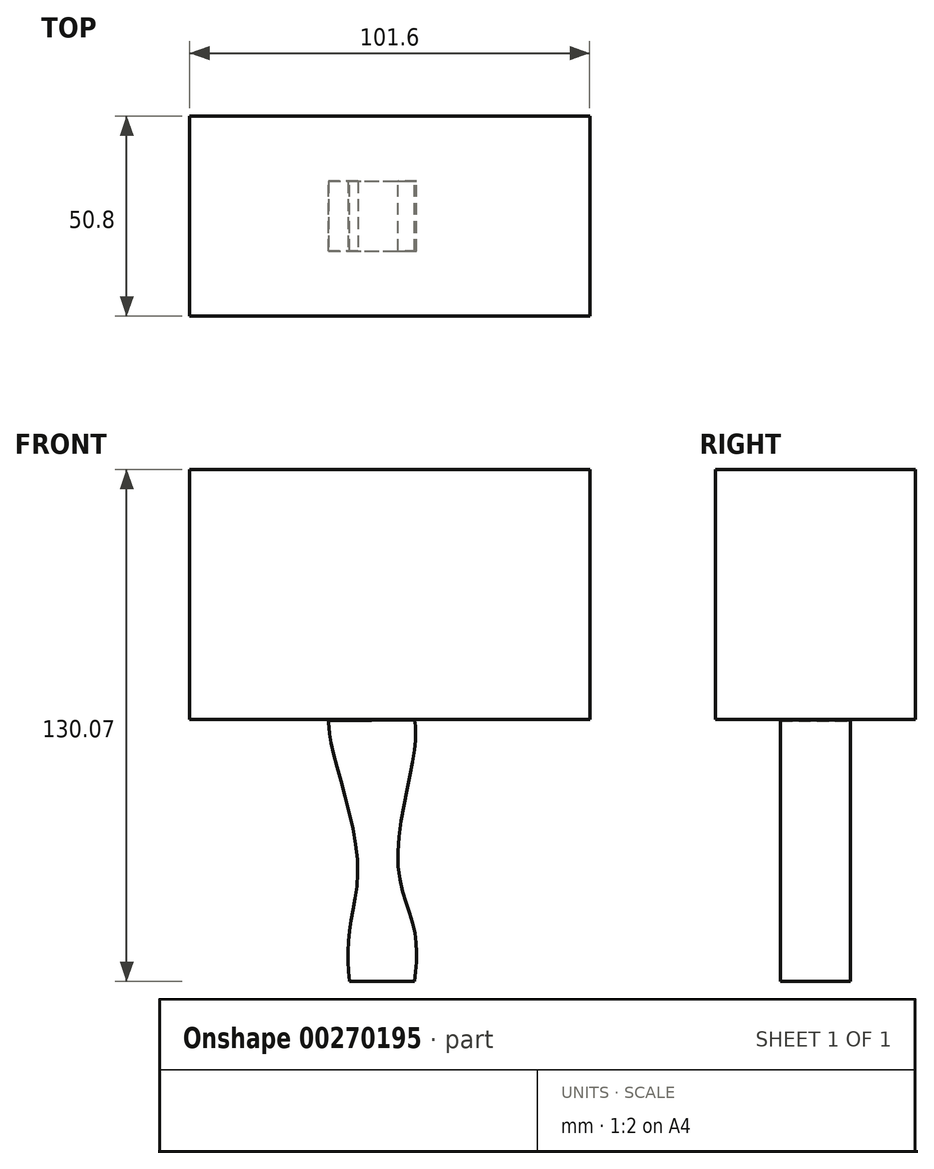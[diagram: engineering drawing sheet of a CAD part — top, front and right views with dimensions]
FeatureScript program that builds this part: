
annotation { "Feature Type Name" : "Feature", "Feature Type Description" : "" }
export const myFeature = defineFeature(function(context is Context, id is Id, definition is map)
    precondition{}
    {
        {
            var Q0;
            Q0=qCreatedBy(makeId("Front.planeOp"),FACE);
            var sketch = newSketch(context, id + "F0", { "sketchPlane" : qUnion([Q0])});
            skLineSegment(sketch, "E0.bottom", {"start": v(-47.1, 68.51) * mm, "end": v(54.5, 68.51) * mm});
            skLineSegment(sketch, "E0.top", {"start": v(-47.1, 5.01) * mm, "end": v(54.5, 5.01) * mm});
            skLineSegment(sketch, "E0.left", {"start": v(-47.1, 68.51) * mm, "end": v(-47.1, 5.01) * mm});
            skLineSegment(sketch, "E0.right", {"start": v(54.5, 68.51) * mm, "end": v(54.5, 5.01) * mm});
            skSolve(sketch);
        }
        {
            var Q0;
            Q0=makeQuery(id+"F0.imprint","IMPRINT",FACE,{"disambiguationData":[TD([[makeQuery(id+"F0.imprint","IMPRINT",EDGE,{"derivedFrom":sQuery(id+"F0.wireOp",EDGE,"E0.bottom")}),-1.0]])]});
            extrude(context, id + "F1", {"entities" : qUnion([Q0]), "endBound" : BoundingType.SYMMETRIC, "depth" : 50.8 * mm});
        }
        {
            var Q0;
            Q0=qCreatedBy(makeId("Front.planeOp"),FACE);
            var sketch = newSketch(context, id + "F2", { "sketchPlane" : qUnion([Q0])});
            skLineSegment(sketch, "E1", {"start": v(-6.6, -61.56) * mm, "end": v(10.02, -61.56) * mm});
            skFitSpline(sketch, "E2", {"points": [v(-6.6, -61.56) * mm, v(-6.6, -48.9) * mm, v(-4.48, -31.24) * mm, v(-10.8, -2.77) * mm, v(-11.86, 4.09) * mm, v(-11.86, 4.61) * mm], "startDerivative": vector(-3.9, 58.02) * mm, "endDerivative": vector(0.31, 9.43) * mm});
            skFitSpline(sketch, "E3", {"points": [v(10.02, -61.56) * mm, v(10.02, -48.9) * mm, v(5.8, -31.5) * mm, v(10.02, -2.77) * mm, v(10.02, 4.88) * mm], "startDerivative": vector(5.81, 56.5) * mm, "endDerivative": vector(-4.18, 35.43) * mm});
            skLineSegment(sketch, "E4", {"start": v(-11.86, 4.61) * mm, "end": v(10.02, 4.88) * mm});
            skSolve(sketch);
        }
        {
            var Q0;
            Q0=makeQuery(id+"F2.imprint","IMPRINT",FACE,{"disambiguationData":[TD([[makeQuery(id+"F2.imprint","IMPRINT",EDGE,{"derivedFrom":sQuery(id+"F2.wireOp",EDGE,"E1")}),1.0]])]});
            extrude(context, id + "F3", {"entities" : qUnion([Q0]), "endBound" : BoundingType.SYMMETRIC, "depth" : 17.78 * mm});
        }
    });
